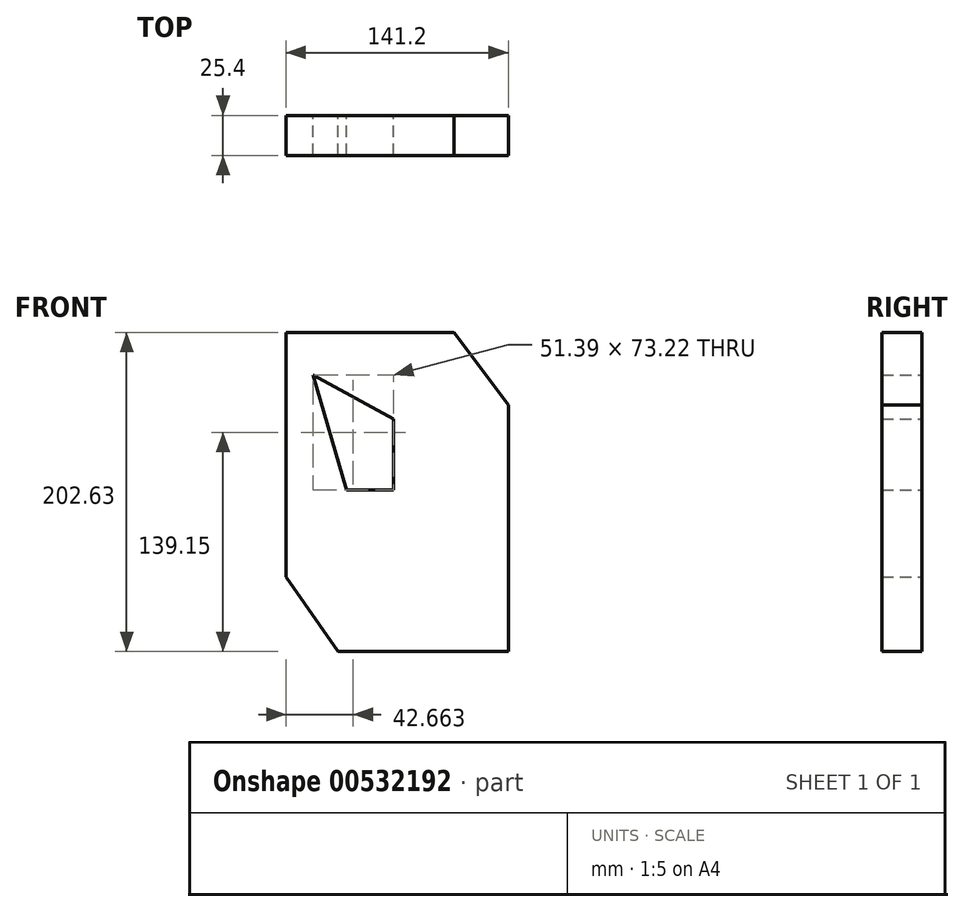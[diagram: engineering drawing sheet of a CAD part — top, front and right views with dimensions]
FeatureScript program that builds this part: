
annotation { "Feature Type Name" : "Feature", "Feature Type Description" : "" }
export const myFeature = defineFeature(function(context is Context, id is Id, definition is map)
    precondition{}
    {
        {
            var Q0;
            Q0=qCreatedBy(makeId("Front.planeOp"),FACE);
            var sketch = newSketch(context, id + "F0", { "sketchPlane" : qUnion([Q0])});
            skLineSegment(sketch, "E0.bottom", {"start": v(53.36, 0) * mm, "end": v(-53.36, 0) * mm});
            skLineSegment(sketch, "E0.top", {"start": v(53.36, 155.1) * mm, "end": v(-53.36, 155.1) * mm});
            skLineSegment(sketch, "E0.left", {"start": v(53.36, 0) * mm, "end": v(53.36, 155.1) * mm});
            skLineSegment(sketch, "E0.right", {"start": v(-53.36, 0) * mm, "end": v(-53.36, 155.1) * mm});
            skPoint(sketch, "E0.middle", {"position": v(0, 77.55) * mm});
            skLineSegment(sketch, "E1.bottom", {"start": v(-15, 55.02) * mm, "end": v(15, 55.02) * mm});
            skLineSegment(sketch, "E1.top", {"start": v(-15, 100.1) * mm, "end": v(15, 100.1) * mm});
            skLineSegment(sketch, "E1.left", {"start": v(-15, 55.02) * mm, "end": v(-15, 100.1) * mm});
            skLineSegment(sketch, "E1.right", {"start": v(15, 55.02) * mm, "end": v(15, 100.1) * mm});
            skLineSegment(sketch, "E2", {"start": v(-15, 55.02) * mm, "end": v(-36.4, 128.24) * mm});
            skLineSegment(sketch, "E3", {"start": v(-36.4, 128.24) * mm, "end": v(15, 55.02) * mm});
            skLineSegment(sketch, "E4", {"start": v(15, 100.1) * mm, "end": v(-36.4, 128.24) * mm});
            skLineSegment(sketch, "E5", {"start": v(-15, 100.1) * mm, "end": v(-36.4, 128.24) * mm});
            skLineSegment(sketch, "E6", {"start": v(53.36, 0) * mm, "end": v(87.84, -47.52) * mm});
            skLineSegment(sketch, "E7", {"start": v(87.84, -47.52) * mm, "end": v(87.84, 108.98) * mm});
            skLineSegment(sketch, "E8", {"start": v(87.84, 108.98) * mm, "end": v(53.36, 155.1) * mm});
            skLineSegment(sketch, "E9", {"start": v(87.84, -47.52) * mm, "end": v(-20.4, -47.52) * mm});
            skLineSegment(sketch, "E10", {"start": v(-20.4, -47.52) * mm, "end": v(-53.36, 0) * mm});
            skSolve(sketch);
        }
        {
            var Q0;
            Q0 = qSketchRegion(id + "F0", true);
            extrude(context, id + "F1", {"entities" : qUnion([Q0]), "depth" : 25.4 * mm, "offsetDistance" : 25.4 * mm});
        }
    });
